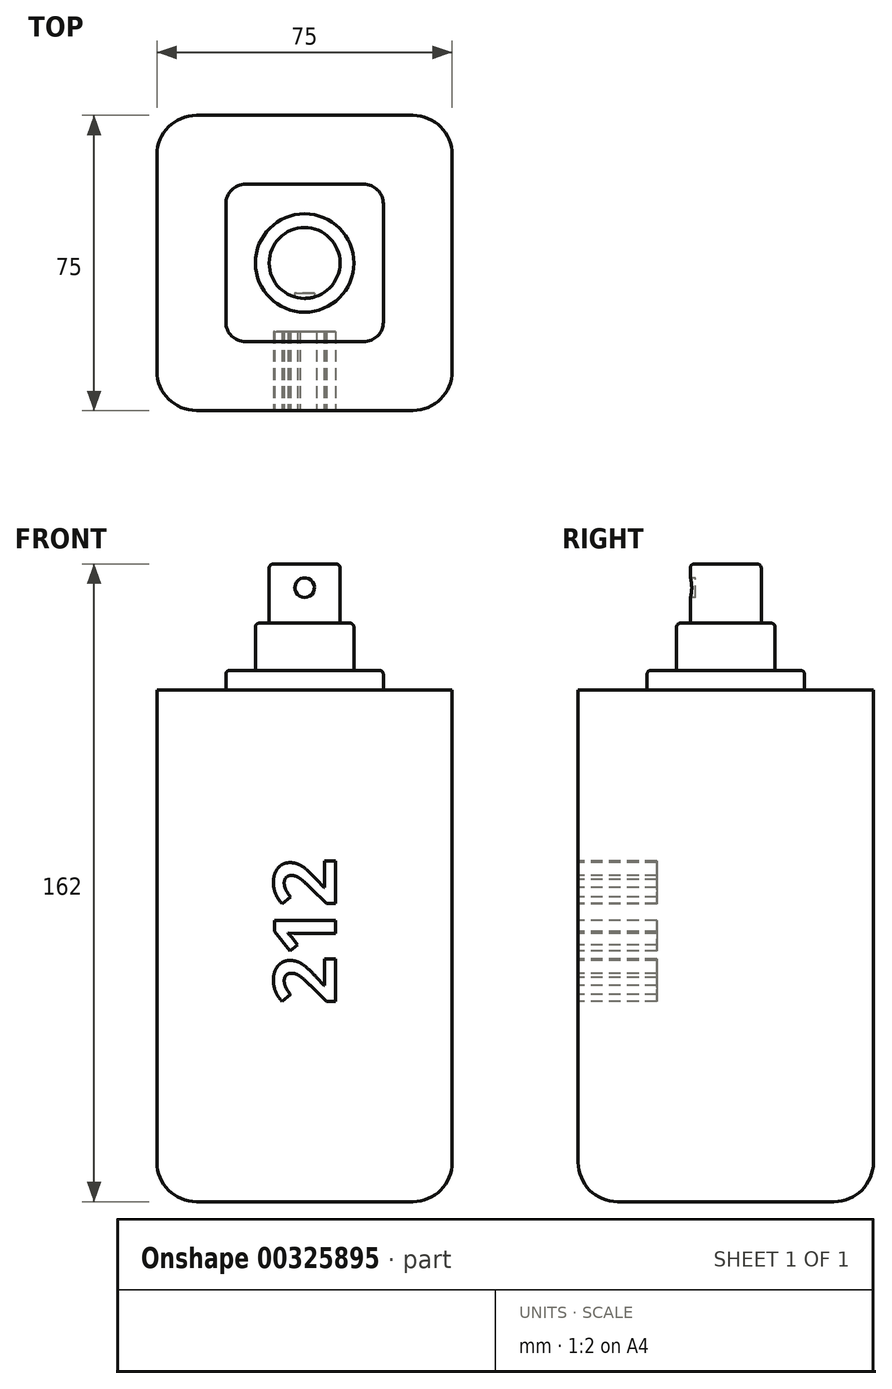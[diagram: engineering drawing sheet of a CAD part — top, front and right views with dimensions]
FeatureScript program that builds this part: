
annotation { "Feature Type Name" : "Feature", "Feature Type Description" : "" }
export const myFeature = defineFeature(function(context is Context, id is Id, definition is map)
    precondition{}
    {
        {
            var Q0;
            Q0=qCreatedBy(makeId("Front.planeOp"),FACE);
            var sketch = newSketch(context, id + "F0", { "sketchPlane" : qUnion([Q0])});
            skLineSegment(sketch, "E0.bottom", {"start": v(-37.5, 90) * mm, "end": v(37.5, 90) * mm});
            skLineSegment(sketch, "E0.top", {"start": v(-37.5, -90) * mm, "end": v(37.5, -90) * mm});
            skLineSegment(sketch, "E0.left", {"start": v(-37.5, 90) * mm, "end": v(-37.5, -90) * mm});
            skLineSegment(sketch, "E0.right", {"start": v(37.5, 90) * mm, "end": v(37.5, -90) * mm});
            skPoint(sketch, "E0.middle", {"position": v(0, 0) * mm});
            skSolve(sketch);
        }
        {
            var Q0;
            Q0 = qSketchRegion(id + "F0", true);
            extrude(context, id + "F1", {"entities" : qUnion([Q0]), "depth" : 75 * mm, "symmetric" : true});
        }
        {
            var Q0;
            Q0=makeQuery(id+"F1.opExtrude","CAP_EDGE",EDGE,{"disambiguationData":[OSD([sQuery(id+"F0.wireOp",EDGE,"E0.bottom")])],"isStart":false});
            var Q1;
            Q1=makeQuery(id+"F1.opExtrude","SWEPT_EDGE",EDGE,{"disambiguationData":[OSD([sQuery(id+"F0.wireOp",EDGE,"E0.bottom"),sQuery(id+"F0.wireOp",EDGE,"E0.right")])]});
            var Q2;
            Q2=makeQuery(id+"F1.opExtrude","CAP_EDGE",EDGE,{"disambiguationData":[OSD([sQuery(id+"F0.wireOp",EDGE,"E0.bottom")])],"isStart":true});
            var Q3;
            Q3=makeQuery(id+"F1.opExtrude","CAP_EDGE",EDGE,{"disambiguationData":[OSD([sQuery(id+"F0.wireOp",EDGE,"E0.left")])],"isStart":false});
            var Q4;
            Q4=makeQuery(id+"F1.opExtrude","SWEPT_EDGE",EDGE,{"disambiguationData":[OSD([sQuery(id+"F0.wireOp",EDGE,"E0.bottom"),sQuery(id+"F0.wireOp",EDGE,"E0.left")])]});
            var Q5;
            Q5=makeQuery(id+"F1.opExtrude","CAP_EDGE",EDGE,{"disambiguationData":[OSD([sQuery(id+"F0.wireOp",EDGE,"E0.left")])],"isStart":true});
            var Q6;
            Q6=makeQuery(id+"F1.opExtrude","CAP_EDGE",EDGE,{"disambiguationData":[OSD([sQuery(id+"F0.wireOp",EDGE,"E0.right")])],"isStart":true});
            var Q7;
            Q7=makeQuery(id+"F1.opExtrude","CAP_EDGE",EDGE,{"disambiguationData":[OSD([sQuery(id+"F0.wireOp",EDGE,"E0.right")])],"isStart":false});
            var Q8;
            Q8=makeQuery(id+"F1.opExtrude","SWEPT_EDGE",EDGE,{"disambiguationData":[OSD([sQuery(id+"F0.wireOp",EDGE,"E0.top"),sQuery(id+"F0.wireOp",EDGE,"E0.left")])]});
            var Q9;
            Q9=makeQuery(id+"F1.opExtrude","CAP_EDGE",EDGE,{"disambiguationData":[OSD([sQuery(id+"F0.wireOp",EDGE,"E0.top")])],"isStart":true});
            var Q10;
            Q10=makeQuery(id+"F1.opExtrude","SWEPT_EDGE",EDGE,{"disambiguationData":[OSD([sQuery(id+"F0.wireOp",EDGE,"E0.top"),sQuery(id+"F0.wireOp",EDGE,"E0.right")])]});
            var Q11;
            Q11=makeQuery(id+"F1.opExtrude","CAP_EDGE",EDGE,{"disambiguationData":[OSD([sQuery(id+"F0.wireOp",EDGE,"E0.top")])],"isStart":false});
            fillet(context, id + "F2", {"entities" : qUnion([Q0, Q1, Q2, Q3, Q4, Q5, Q6, Q7, Q8, Q9, Q10, Q11]), "radius" : 10 * mm, "tangentPropagation" : true, "allowEdgeOverflow" : false});
        }
        {
            var Q0;
            Q0=qCreatedBy(makeId("Front.planeOp"),FACE);
            cPlane(context, id + "F3", {"entities" : qUnion([Q0]), "cplaneType" : CPlaneType.OFFSET, "offset" : 101 * mm, "width" : 150 * mm, "height" : 150 * mm});
        }
        {
            var Q0;
            Q0=qCreatedBy(id+"F3.planeOp",FACE);
            var sketch = newSketch(context, id + "F4", { "sketchPlane" : qUnion([Q0])});
            skLineSegment(sketch, "E1.bottom", {"start": v(-103.01, 113.49) * mm, "end": v(143.96, 113.49) * mm});
            skLineSegment(sketch, "E1.top", {"start": v(-103.01, 40) * mm, "end": v(143.96, 40) * mm});
            skLineSegment(sketch, "E1.left", {"start": v(-103.01, 113.49) * mm, "end": v(-103.01, 40) * mm});
            skLineSegment(sketch, "E1.right", {"start": v(143.96, 113.49) * mm, "end": v(143.96, 40) * mm});
            skSolve(sketch);
        }
        {
            var Q0;
            Q0 = qSketchRegion(id + "F4", true);
            extrude(context, id + "F5", {"entities" : qUnion([Q0]), "operationType" : NewBodyOperationType.REMOVE, "endBound" : BoundingType.THROUGH_ALL, "oppositeDirection" : true, "depth" : 25 * mm});
        }
        {
            var Q0;
            Q0=makeQuery(id+"F5.boolean.opBoolean","COPY",FACE,{"derivedFrom":makeQuery(id+"F5.opExtrude","SWEPT_FACE",FACE,{"disambiguationData":[OSD([sQuery(id+"F4.wireOp",EDGE,"E1.top")])]})});
            var sketch = newSketch(context, id + "F6", { "sketchPlane" : qUnion([Q0])});
            skLineSegment(sketch, "E2.bottom", {"start": v(-20, 20) * mm, "end": v(20, 20) * mm});
            skLineSegment(sketch, "E2.top", {"start": v(-20, -20) * mm, "end": v(20, -20) * mm});
            skLineSegment(sketch, "E2.left", {"start": v(-20, 20) * mm, "end": v(-20, -20) * mm});
            skLineSegment(sketch, "E2.right", {"start": v(20, 20) * mm, "end": v(20, -20) * mm});
            skPoint(sketch, "E2.middle", {"position": v(0, 0) * mm});
            skSolve(sketch);
        }
        {
            var Q0;
            Q0 = qSketchRegion(id + "F6", true);
            extrude(context, id + "F7", {"entities" : qUnion([Q0]), "operationType" : NewBodyOperationType.ADD, "depth" : 5 * mm});
        }
        {
            var Q0;
            Q0=makeQuery(id+"F7.opExtrude","SWEPT_EDGE",EDGE,{"disambiguationData":[OSD([sQuery(id+"F6.wireOp",EDGE,"E2.bottom"),sQuery(id+"F6.wireOp",EDGE,"E2.right")])]});
            var Q1;
            Q1=makeQuery(id+"F7.opExtrude","SWEPT_EDGE",EDGE,{"disambiguationData":[OSD([sQuery(id+"F6.wireOp",EDGE,"E2.top"),sQuery(id+"F6.wireOp",EDGE,"E2.right")])]});
            var Q2;
            Q2=makeQuery(id+"F7.opExtrude","SWEPT_EDGE",EDGE,{"disambiguationData":[OSD([sQuery(id+"F6.wireOp",EDGE,"E2.bottom"),sQuery(id+"F6.wireOp",EDGE,"E2.left")])]});
            var Q3;
            Q3=makeQuery(id+"F7.opExtrude","SWEPT_EDGE",EDGE,{"disambiguationData":[OSD([sQuery(id+"F6.wireOp",EDGE,"E2.top"),sQuery(id+"F6.wireOp",EDGE,"E2.left")])]});
            fillet(context, id + "F8", {"entities" : qUnion([Q0, Q1, Q2, Q3]), "radius" : 5 * mm, "tangentPropagation" : true, "allowEdgeOverflow" : false});
        }
        {
            var Q0;
            Q0=makeQuery(id+"F7.opExtrude","CAP_FACE",FACE,{"disambiguationData":[OSD([sQuery(id+"F6.wireOp",EDGE,"E2.bottom"),sQuery(id+"F6.wireOp",EDGE,"E2.top"),sQuery(id+"F6.wireOp",EDGE,"E2.left"),sQuery(id+"F6.wireOp",EDGE,"E2.right")])],"isStart":false});
            var sketch = newSketch(context, id + "F9", { "sketchPlane" : qUnion([Q0])});
            skCircle(sketch, "E3", {"center": v(0, 0) * mm, "radius": 12.5 * mm});
            skSolve(sketch);
        }
        {
            var Q0;
            Q0 = qSketchRegion(id + "F9", true);
            extrude(context, id + "F10", {"entities" : qUnion([Q0]), "operationType" : NewBodyOperationType.ADD, "depth" : 12 * mm});
        }
        {
            var Q0;
            Q0=makeQuery(id+"F10.opExtrude","CAP_FACE",FACE,{"disambiguationData":[OSD([sQuery(id+"F9.wireOp",EDGE,"E3")])],"isStart":false});
            var sketch = newSketch(context, id + "F11", { "sketchPlane" : qUnion([Q0])});
            skCircle(sketch, "E4", {"center": v(0, 0) * mm, "radius": 9 * mm});
            skSolve(sketch);
        }
        {
            var Q0;
            Q0 = qSketchRegion(id + "F11", true);
            extrude(context, id + "F12", {"entities" : qUnion([Q0]), "operationType" : NewBodyOperationType.ADD, "depth" : 15 * mm});
        }
        {
            var Q0;
            Q0=makeQuery(id+"F7.opExtrude","CAP_EDGE",EDGE,{"disambiguationData":[OSD([sQuery(id+"F6.wireOp",EDGE,"E2.left")])],"isStart":false});
            var Q1;
            Q1=makeQuery(id+"F10.opExtrude","CAP_EDGE",EDGE,{"disambiguationData":[OSD([sQuery(id+"F9.wireOp",EDGE,"E3")])],"isStart":false});
            var Q2;
            Q2=makeQuery(id+"F12.opExtrude","CAP_EDGE",EDGE,{"disambiguationData":[OSD([sQuery(id+"F11.wireOp",EDGE,"E4")])],"isStart":false});
            fillet(context, id + "F13", {"entities" : qUnion([Q0, Q1, Q2]), "radius" : 1 * mm, "tangentPropagation" : true, "allowEdgeOverflow" : false});
        }
        {
            var Q0;
            Q0=qCreatedBy(id+"F3.planeOp",FACE);
            var sketch = newSketch(context, id + "F14", { "sketchPlane" : qUnion([Q0])});
            skCircle(sketch, "E5", {"center": v(0, 66) * mm, "radius": 2.5 * mm});
            skSolve(sketch);
        }
        {
            var Q0;
            Q0 = qSketchRegion(id + "F14", true);
            extrude(context, id + "F15", {"entities" : qUnion([Q0]), "operationType" : NewBodyOperationType.REMOVE, "oppositeDirection" : true, "depth" : 93.3 * mm});
        }
        {
            var Q0;
            Q0=qCreatedBy(id+"F3.planeOp",FACE);
            var sketch = newSketch(context, id + "F16", { "sketchPlane" : qUnion([Q0])});
            skLineSegment(sketch, "E6.bottom", {"start": v(-10, -40) * mm, "end": v(10, -40) * mm});
            skLineSegment(sketch, "E6.top", {"start": v(-10, -2) * mm, "end": v(10, -2) * mm});
            skLineSegment(sketch, "E6.left", {"start": v(-10, -40) * mm, "end": v(-10, -2) * mm});
            skLineSegment(sketch, "E6.right", {"start": v(10, -40) * mm, "end": v(10, -2) * mm});
            skPoint(sketch, "E6.middle", {"position": v(0, -21) * mm});
            skText(sketch, "E7", { "text": "212", "fontName": "OpenSans-Bold.ttf"});
            skPoint(sketch, "E8", {"position": v(0, -2) * mm});
            const initialGuessF16  = {"E7": [0.00784, -0.04, 0, 1, 0.01567]};
            skSetInitialGuess(sketch, initialGuessF16);
            skSolve(sketch);
        }
        {
            var Q0;
            Q0=makeQuery(id+"F16.imprint","IMPRINT",FACE,{"disambiguationData":[TD([[makeQuery(id+"F16.imprint","IMPRINT",EDGE,{"derivedFrom":sQuery(id+"F16.wireOp",EDGE,"E7.sketch_text.stroke-34")}),-1.0]])]});
            var Q1;
            Q1=makeQuery(id+"F16.imprint","IMPRINT",FACE,{"disambiguationData":[TD([[makeQuery(id+"F16.imprint","IMPRINT",EDGE,{"derivedFrom":sQuery(id+"F16.wireOp",EDGE,"E7.sketch_text.stroke-0")}),-1.0]])]});
            var Q2;
            Q2=makeQuery(id+"F16.imprint","IMPRINT",FACE,{"disambiguationData":[TD([[makeQuery(id+"F16.imprint","IMPRINT",EDGE,{"derivedFrom":sQuery(id+"F16.wireOp",EDGE,"E7.sketch_text.stroke-24")}),-1.0]])]});
            extrude(context, id + "F17", {"entities" : qUnion([Q0, Q1, Q2]), "operationType" : NewBodyOperationType.REMOVE, "oppositeDirection" : true, "depth" : 83.5 * mm});
        }
    });
